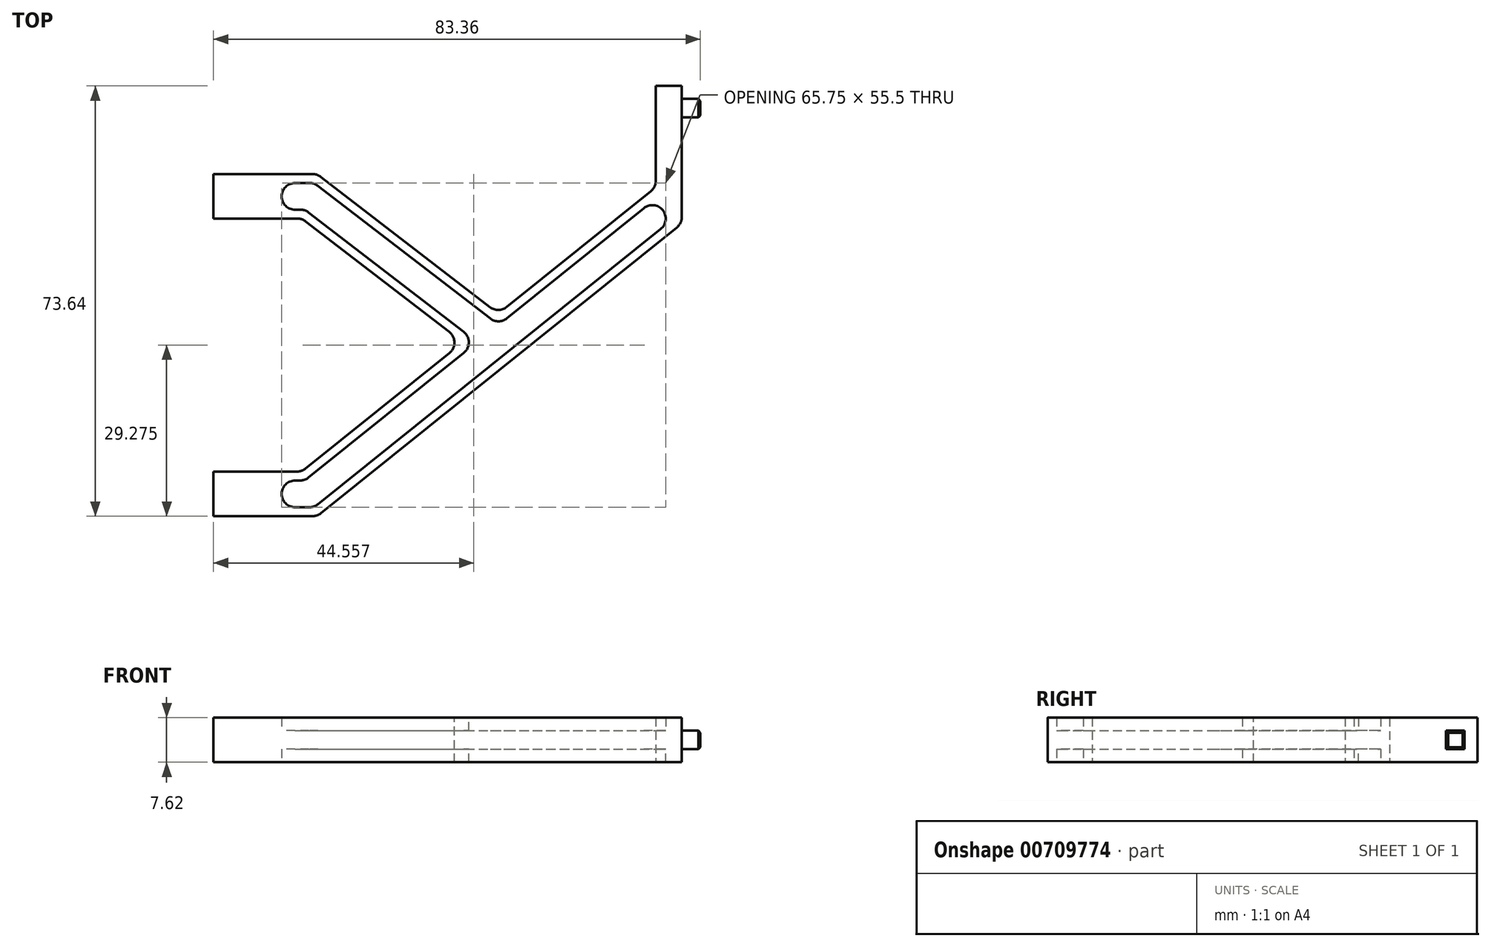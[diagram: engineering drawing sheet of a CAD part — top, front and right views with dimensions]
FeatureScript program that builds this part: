
annotation { "Feature Type Name" : "Feature", "Feature Type Description" : "" }
export const myFeature = defineFeature(function(context is Context, id is Id, definition is map)
    precondition{}
    {
        {
            var Q0;
            Q0=qCreatedBy(makeId("Top.planeOp"),FACE);
            var sketch = newSketch(context, id + "F0", { "sketchPlane" : qUnion([Q0])});
            skLineSegment(sketch, "E0", {"start": v(0, 10.36) * mm, "end": v(17.78, 10.36) * mm});
            skLineSegment(sketch, "E1", {"start": v(0, 68.9) * mm, "end": v(17.78, 68.9) * mm});
            skLineSegment(sketch, "E2", {"start": v(17.78, 68.9) * mm, "end": v(48.79, 45.03) * mm});
            skLineSegment(sketch, "E3", {"start": v(17.78, 10.36) * mm, "end": v(80.19, 60.46) * mm});
            skLineSegment(sketch, "E4", {"start": v(0, 10.36) * mm, "end": v(0, 17.98) * mm});
            skLineSegment(sketch, "E5", {"start": v(17.78, 20.13) * mm, "end": v(42.67, 40.12) * mm});
            skLineSegment(sketch, "E6", {"start": v(0, 68.9) * mm, "end": v(0, 61.29) * mm});
            skLineSegment(sketch, "E7", {"start": v(15.5, 61.04) * mm, "end": v(42.67, 40.12) * mm});
            skLineSegment(sketch, "E8", {"start": v(0, 17.98) * mm, "end": v(15.1, 17.98) * mm});
            skLineSegment(sketch, "E9", {"start": v(17.78, 20.13) * mm, "end": v(15.1, 17.98) * mm});
            skLineSegment(sketch, "E10", {"start": v(15.5, 61.04) * mm, "end": v(15.19, 61.29) * mm});
            skLineSegment(sketch, "E11", {"start": v(0, 61.29) * mm, "end": v(15.19, 61.29) * mm});
            skLineSegment(sketch, "E12", {"start": v(75.74, 84) * mm, "end": v(75.74, 66.67) * mm});
            skLineSegment(sketch, "E13.trimOffspring", {"start": v(48.79, 45.03) * mm, "end": v(75.74, 66.67) * mm});
            skLineSegment(sketch, "E14", {"start": v(75.74, 84) * mm, "end": v(80.19, 84) * mm});
            skLineSegment(sketch, "E15", {"start": v(17.26, 67.38) * mm, "end": v(48.8, 43.09) * mm});
            skLineSegment(sketch, "E16", {"start": v(15.7, 62.81) * mm, "end": v(45.14, 40.14) * mm});
            skLineSegment(sketch, "E17", {"start": v(11.68, 67.38) * mm, "end": v(17.26, 67.38) * mm});
            skLineSegment(sketch, "E18", {"start": v(11.68, 62.81) * mm, "end": v(15.7, 62.81) * mm});
            skLineSegment(sketch, "E19", {"start": v(80.19, 84) * mm, "end": v(80.19, 60.46) * mm});
            skLineSegment(sketch, "E20.trimOffspring", {"start": v(11.68, 67.38) * mm, "end": v(11.68, 62.81) * mm});
            skLineSegment(sketch, "E21", {"start": v(15.64, 16.46) * mm, "end": v(45.14, 40.14) * mm});
            skLineSegment(sketch, "E22", {"start": v(17.24, 11.89) * mm, "end": v(78.37, 60.96) * mm});
            skLineSegment(sketch, "E23", {"start": v(11.68, 16.46) * mm, "end": v(15.64, 16.46) * mm});
            skLineSegment(sketch, "E24", {"start": v(11.68, 11.89) * mm, "end": v(17.24, 11.89) * mm});
            skLineSegment(sketch, "E25", {"start": v(11.68, 16.46) * mm, "end": v(11.68, 11.89) * mm});
            skLineSegment(sketch, "E26.trimOffspring", {"start": v(48.8, 43.09) * mm, "end": v(75.5, 64.53) * mm});
            skLineSegment(sketch, "E27.trimOffspring", {"start": v(75.5, 64.53) * mm, "end": v(78.37, 60.96) * mm});
            skLineSegment(sketch, "E28", {"start": v(80.19, 81.78) * mm, "end": v(83.36, 81.78) * mm});
            skLineSegment(sketch, "E29", {"start": v(83.36, 81.78) * mm, "end": v(83.36, 78.6) * mm});
            skLineSegment(sketch, "E30", {"start": v(83.36, 78.6) * mm, "end": v(80.19, 78.6) * mm});
            skSolve(sketch);
        }
        {
            var Q0;
            Q0=makeQuery(id+"F0.imprint","IMPRINT",FACE,{"disambiguationData":[TD([[makeQuery(id+"F0.imprint","IMPRINT",EDGE,{"derivedFrom":sQuery(id+"F0.wireOp",EDGE,"E0")}),1.0]])]});
            extrude(context, id + "F1", {"entities" : qUnion([Q0]), "depth" : 7.62 * mm, "offsetDistance" : 25.4 * mm, "symmetric" : true});
        }
        {
            var Q0;
            Q0=makeQuery(id+"F0.imprint","IMPRINT",FACE,{"disambiguationData":[TD([[makeQuery(id+"F0.imprint","IMPRINT",EDGE,{"derivedFrom":sQuery(id+"F0.wireOp",EDGE,"E15")}),-1.0]])]});
            extrude(context, id + "F2", {"entities" : qUnion([Q0]), "operationType" : NewBodyOperationType.ADD, "depth" : 3.17 * mm, "offsetDistance" : 25.4 * mm, "symmetric" : true});
        }
        {
            var Q0;
            {var subQ0=sQuery(id+"F0.wireOp",EDGE,"E28");Q0=makeQuery(id+"F0.imprint","IMPRINT",FACE,{"disambiguationData":[TD([[makeQuery(id+"F0.imprint","IMPRINT",EDGE,{"derivedFrom":subQ0}),-1.0]])]});}
            extrude(context, id + "F3", {"entities" : qUnion([Q0]), "operationType" : NewBodyOperationType.ADD, "depth" : 3.17 * mm, "offsetDistance" : 25.4 * mm, "symmetric" : true});
        }
        {
            var Q0;
            Q0=makeQuery(id+"F1.opExtrude","SWEPT_EDGE",EDGE,{"disambiguationData":[OSD([sQuery(id+"F0.wireOp",EDGE,"E10"),sQuery(id+"F0.wireOp",EDGE,"E11")])]});
            var Q1;
            {var subQ0=sQuery(id+"F0.wireOp",EDGE,"E27.trimOffspring");var subQ1=sQuery(id+"F0.wireOp",EDGE,"E26.trimOffspring");var subQ2=sQuery(id+"F0.wireOp",EDGE,"E25");var subQ3=sQuery(id+"F0.wireOp",EDGE,"E24");var subQ4=sQuery(id+"F0.wireOp",EDGE,"E23");var subQ5=sQuery(id+"F0.wireOp",EDGE,"E22");var subQ6=sQuery(id+"F0.wireOp",EDGE,"E21");var subQ7=sQuery(id+"F0.wireOp",EDGE,"E20.trimOffspring");var subQ8=sQuery(id+"F0.wireOp",EDGE,"E18");var subQ9=sQuery(id+"F0.wireOp",EDGE,"E17");var subQ10=sQuery(id+"F0.wireOp",EDGE,"E16");var subQ11=sQuery(id+"F0.wireOp",EDGE,"E15");Q1=makeQuery(id+"F2.boolean.opBoolean","SPLIT",EDGE,{"disambiguationData":[TD([makeQuery(id+"F2.opExtrude","CAP_FACE",FACE,{"disambiguationData":[OSD([subQ11,subQ10,subQ9,subQ8,subQ7,subQ6,subQ5,subQ4,subQ3,subQ2,subQ1,subQ0])],"isStart":false})])],"derivedFrom":makeQuery(id+"F1.opExtrude","SWEPT_EDGE",EDGE,{"disambiguationData":[OSD([subQ8,subQ7])]})});}
            var Q2;
            {var subQ0=sQuery(id+"F0.wireOp",EDGE,"E27.trimOffspring");var subQ1=sQuery(id+"F0.wireOp",EDGE,"E26.trimOffspring");var subQ2=sQuery(id+"F0.wireOp",EDGE,"E25");var subQ3=sQuery(id+"F0.wireOp",EDGE,"E24");var subQ4=sQuery(id+"F0.wireOp",EDGE,"E23");var subQ5=sQuery(id+"F0.wireOp",EDGE,"E22");var subQ6=sQuery(id+"F0.wireOp",EDGE,"E21");var subQ7=sQuery(id+"F0.wireOp",EDGE,"E20.trimOffspring");var subQ8=sQuery(id+"F0.wireOp",EDGE,"E18");var subQ9=sQuery(id+"F0.wireOp",EDGE,"E17");var subQ10=sQuery(id+"F0.wireOp",EDGE,"E16");var subQ11=sQuery(id+"F0.wireOp",EDGE,"E15");Q2=makeQuery(id+"F2.boolean.opBoolean","SPLIT",EDGE,{"disambiguationData":[TD([makeQuery(id+"F2.opExtrude","CAP_FACE",FACE,{"disambiguationData":[OSD([subQ11,subQ10,subQ9,subQ8,subQ7,subQ6,subQ5,subQ4,subQ3,subQ2,subQ1,subQ0])],"isStart":false})])],"derivedFrom":makeQuery(id+"F1.opExtrude","SWEPT_EDGE",EDGE,{"disambiguationData":[OSD([subQ10,subQ8])]})});}
            var Q3;
            {var subQ0=sQuery(id+"F0.wireOp",EDGE,"E27.trimOffspring");var subQ1=sQuery(id+"F0.wireOp",EDGE,"E26.trimOffspring");var subQ2=sQuery(id+"F0.wireOp",EDGE,"E25");var subQ3=sQuery(id+"F0.wireOp",EDGE,"E24");var subQ4=sQuery(id+"F0.wireOp",EDGE,"E23");var subQ5=sQuery(id+"F0.wireOp",EDGE,"E22");var subQ6=sQuery(id+"F0.wireOp",EDGE,"E21");var subQ7=sQuery(id+"F0.wireOp",EDGE,"E20.trimOffspring");var subQ8=sQuery(id+"F0.wireOp",EDGE,"E18");var subQ9=sQuery(id+"F0.wireOp",EDGE,"E17");var subQ10=sQuery(id+"F0.wireOp",EDGE,"E16");var subQ11=sQuery(id+"F0.wireOp",EDGE,"E15");Q3=makeQuery(id+"F2.boolean.opBoolean","SPLIT",EDGE,{"disambiguationData":[TD([makeQuery(id+"F2.opExtrude","CAP_FACE",FACE,{"disambiguationData":[OSD([subQ11,subQ10,subQ9,subQ8,subQ7,subQ6,subQ5,subQ4,subQ3,subQ2,subQ1,subQ0])],"isStart":false})])],"derivedFrom":makeQuery(id+"F1.opExtrude","SWEPT_EDGE",EDGE,{"disambiguationData":[OSD([subQ9,subQ7])]})});}
            var Q4;
            {var subQ0=sQuery(id+"F0.wireOp",EDGE,"E27.trimOffspring");var subQ1=sQuery(id+"F0.wireOp",EDGE,"E26.trimOffspring");var subQ2=sQuery(id+"F0.wireOp",EDGE,"E25");var subQ3=sQuery(id+"F0.wireOp",EDGE,"E24");var subQ4=sQuery(id+"F0.wireOp",EDGE,"E23");var subQ5=sQuery(id+"F0.wireOp",EDGE,"E22");var subQ6=sQuery(id+"F0.wireOp",EDGE,"E21");var subQ7=sQuery(id+"F0.wireOp",EDGE,"E20.trimOffspring");var subQ8=sQuery(id+"F0.wireOp",EDGE,"E18");var subQ9=sQuery(id+"F0.wireOp",EDGE,"E17");var subQ10=sQuery(id+"F0.wireOp",EDGE,"E16");var subQ11=sQuery(id+"F0.wireOp",EDGE,"E15");Q4=makeQuery(id+"F2.boolean.opBoolean","SPLIT",EDGE,{"disambiguationData":[TD([makeQuery(id+"F2.opExtrude","CAP_FACE",FACE,{"disambiguationData":[OSD([subQ11,subQ10,subQ9,subQ8,subQ7,subQ6,subQ5,subQ4,subQ3,subQ2,subQ1,subQ0])],"isStart":false})])],"derivedFrom":makeQuery(id+"F1.opExtrude","SWEPT_EDGE",EDGE,{"disambiguationData":[OSD([subQ11,subQ9])]})});}
            var Q5;
            Q5=makeQuery(id+"F1.opExtrude","SWEPT_EDGE",EDGE,{"disambiguationData":[OSD([sQuery(id+"F0.wireOp",EDGE,"E1"),sQuery(id+"F0.wireOp",EDGE,"E2")])]});
            var Q6;
            {var subQ0=sQuery(id+"F0.wireOp",EDGE,"E27.trimOffspring");var subQ1=sQuery(id+"F0.wireOp",EDGE,"E26.trimOffspring");var subQ2=sQuery(id+"F0.wireOp",EDGE,"E25");var subQ3=sQuery(id+"F0.wireOp",EDGE,"E24");var subQ4=sQuery(id+"F0.wireOp",EDGE,"E23");var subQ5=sQuery(id+"F0.wireOp",EDGE,"E22");var subQ6=sQuery(id+"F0.wireOp",EDGE,"E21");var subQ7=sQuery(id+"F0.wireOp",EDGE,"E20.trimOffspring");var subQ8=sQuery(id+"F0.wireOp",EDGE,"E18");var subQ9=sQuery(id+"F0.wireOp",EDGE,"E17");var subQ10=sQuery(id+"F0.wireOp",EDGE,"E16");var subQ11=sQuery(id+"F0.wireOp",EDGE,"E15");Q6=makeQuery(id+"F2.boolean.opBoolean","SPLIT",EDGE,{"disambiguationData":[TD([makeQuery(id+"F2.opExtrude","CAP_FACE",FACE,{"disambiguationData":[OSD([subQ11,subQ10,subQ9,subQ8,subQ7,subQ6,subQ5,subQ4,subQ3,subQ2,subQ1,subQ0])],"isStart":true})])],"derivedFrom":makeQuery(id+"F1.opExtrude","SWEPT_EDGE",EDGE,{"disambiguationData":[OSD([subQ10,subQ8])]})});}
            var Q7;
            {var subQ0=sQuery(id+"F0.wireOp",EDGE,"E27.trimOffspring");var subQ1=sQuery(id+"F0.wireOp",EDGE,"E26.trimOffspring");var subQ2=sQuery(id+"F0.wireOp",EDGE,"E25");var subQ3=sQuery(id+"F0.wireOp",EDGE,"E24");var subQ4=sQuery(id+"F0.wireOp",EDGE,"E23");var subQ5=sQuery(id+"F0.wireOp",EDGE,"E22");var subQ6=sQuery(id+"F0.wireOp",EDGE,"E21");var subQ7=sQuery(id+"F0.wireOp",EDGE,"E20.trimOffspring");var subQ8=sQuery(id+"F0.wireOp",EDGE,"E18");var subQ9=sQuery(id+"F0.wireOp",EDGE,"E17");var subQ10=sQuery(id+"F0.wireOp",EDGE,"E16");var subQ11=sQuery(id+"F0.wireOp",EDGE,"E15");Q7=makeQuery(id+"F2.boolean.opBoolean","SPLIT",EDGE,{"disambiguationData":[TD([makeQuery(id+"F2.opExtrude","CAP_FACE",FACE,{"disambiguationData":[OSD([subQ11,subQ10,subQ9,subQ8,subQ7,subQ6,subQ5,subQ4,subQ3,subQ2,subQ1,subQ0])],"isStart":true})])],"derivedFrom":makeQuery(id+"F1.opExtrude","SWEPT_EDGE",EDGE,{"disambiguationData":[OSD([subQ8,subQ7])]})});}
            var Q8;
            {var subQ0=sQuery(id+"F0.wireOp",EDGE,"E27.trimOffspring");var subQ1=sQuery(id+"F0.wireOp",EDGE,"E26.trimOffspring");var subQ2=sQuery(id+"F0.wireOp",EDGE,"E25");var subQ3=sQuery(id+"F0.wireOp",EDGE,"E24");var subQ4=sQuery(id+"F0.wireOp",EDGE,"E23");var subQ5=sQuery(id+"F0.wireOp",EDGE,"E22");var subQ6=sQuery(id+"F0.wireOp",EDGE,"E21");var subQ7=sQuery(id+"F0.wireOp",EDGE,"E20.trimOffspring");var subQ8=sQuery(id+"F0.wireOp",EDGE,"E18");var subQ9=sQuery(id+"F0.wireOp",EDGE,"E17");var subQ10=sQuery(id+"F0.wireOp",EDGE,"E16");var subQ11=sQuery(id+"F0.wireOp",EDGE,"E15");Q8=makeQuery(id+"F2.boolean.opBoolean","SPLIT",EDGE,{"disambiguationData":[TD([makeQuery(id+"F2.opExtrude","CAP_FACE",FACE,{"disambiguationData":[OSD([subQ11,subQ10,subQ9,subQ8,subQ7,subQ6,subQ5,subQ4,subQ3,subQ2,subQ1,subQ0])],"isStart":true})])],"derivedFrom":makeQuery(id+"F1.opExtrude","SWEPT_EDGE",EDGE,{"disambiguationData":[OSD([subQ9,subQ7])]})});}
            var Q9;
            {var subQ0=sQuery(id+"F0.wireOp",EDGE,"E27.trimOffspring");var subQ1=sQuery(id+"F0.wireOp",EDGE,"E26.trimOffspring");var subQ2=sQuery(id+"F0.wireOp",EDGE,"E25");var subQ3=sQuery(id+"F0.wireOp",EDGE,"E24");var subQ4=sQuery(id+"F0.wireOp",EDGE,"E23");var subQ5=sQuery(id+"F0.wireOp",EDGE,"E22");var subQ6=sQuery(id+"F0.wireOp",EDGE,"E21");var subQ7=sQuery(id+"F0.wireOp",EDGE,"E20.trimOffspring");var subQ8=sQuery(id+"F0.wireOp",EDGE,"E18");var subQ9=sQuery(id+"F0.wireOp",EDGE,"E17");var subQ10=sQuery(id+"F0.wireOp",EDGE,"E16");var subQ11=sQuery(id+"F0.wireOp",EDGE,"E15");Q9=makeQuery(id+"F2.boolean.opBoolean","SPLIT",EDGE,{"disambiguationData":[TD([makeQuery(id+"F2.opExtrude","CAP_FACE",FACE,{"disambiguationData":[OSD([subQ11,subQ10,subQ9,subQ8,subQ7,subQ6,subQ5,subQ4,subQ3,subQ2,subQ1,subQ0])],"isStart":true})])],"derivedFrom":makeQuery(id+"F1.opExtrude","SWEPT_EDGE",EDGE,{"disambiguationData":[OSD([subQ11,subQ9])]})});}
            var Q10;
            {var subQ0=sQuery(id+"F0.wireOp",EDGE,"E27.trimOffspring");var subQ1=sQuery(id+"F0.wireOp",EDGE,"E26.trimOffspring");var subQ2=sQuery(id+"F0.wireOp",EDGE,"E25");var subQ3=sQuery(id+"F0.wireOp",EDGE,"E24");var subQ4=sQuery(id+"F0.wireOp",EDGE,"E23");var subQ5=sQuery(id+"F0.wireOp",EDGE,"E22");var subQ6=sQuery(id+"F0.wireOp",EDGE,"E21");var subQ7=sQuery(id+"F0.wireOp",EDGE,"E20.trimOffspring");var subQ8=sQuery(id+"F0.wireOp",EDGE,"E18");var subQ9=sQuery(id+"F0.wireOp",EDGE,"E17");var subQ10=sQuery(id+"F0.wireOp",EDGE,"E16");var subQ11=sQuery(id+"F0.wireOp",EDGE,"E15");Q10=makeQuery(id+"F2.boolean.opBoolean","SPLIT",EDGE,{"disambiguationData":[TD([makeQuery(id+"F2.opExtrude","CAP_FACE",FACE,{"disambiguationData":[OSD([subQ11,subQ10,subQ9,subQ8,subQ7,subQ6,subQ5,subQ4,subQ3,subQ2,subQ1,subQ0])],"isStart":false})])],"derivedFrom":makeQuery(id+"F1.opExtrude","SWEPT_EDGE",EDGE,{"disambiguationData":[OSD([subQ11,subQ1])]})});}
            var Q11;
            {var subQ0=sQuery(id+"F0.wireOp",EDGE,"E27.trimOffspring");var subQ1=sQuery(id+"F0.wireOp",EDGE,"E26.trimOffspring");var subQ2=sQuery(id+"F0.wireOp",EDGE,"E25");var subQ3=sQuery(id+"F0.wireOp",EDGE,"E24");var subQ4=sQuery(id+"F0.wireOp",EDGE,"E23");var subQ5=sQuery(id+"F0.wireOp",EDGE,"E22");var subQ6=sQuery(id+"F0.wireOp",EDGE,"E21");var subQ7=sQuery(id+"F0.wireOp",EDGE,"E20.trimOffspring");var subQ8=sQuery(id+"F0.wireOp",EDGE,"E18");var subQ9=sQuery(id+"F0.wireOp",EDGE,"E17");var subQ10=sQuery(id+"F0.wireOp",EDGE,"E16");var subQ11=sQuery(id+"F0.wireOp",EDGE,"E15");Q11=makeQuery(id+"F2.boolean.opBoolean","SPLIT",EDGE,{"disambiguationData":[TD([makeQuery(id+"F2.opExtrude","CAP_FACE",FACE,{"disambiguationData":[OSD([subQ11,subQ10,subQ9,subQ8,subQ7,subQ6,subQ5,subQ4,subQ3,subQ2,subQ1,subQ0])],"isStart":false})])],"derivedFrom":makeQuery(id+"F1.opExtrude","SWEPT_EDGE",EDGE,{"disambiguationData":[OSD([subQ10,subQ6])]})});}
            var Q12;
            Q12=makeQuery(id+"F1.opExtrude","SWEPT_EDGE",EDGE,{"disambiguationData":[OSD([sQuery(id+"F0.wireOp",EDGE,"E5"),sQuery(id+"F0.wireOp",EDGE,"E7")])]});
            var Q13;
            Q13=makeQuery(id+"F1.opExtrude","SWEPT_EDGE",EDGE,{"disambiguationData":[OSD([sQuery(id+"F0.wireOp",EDGE,"E2"),sQuery(id+"F0.wireOp",EDGE,"E13.trimOffspring")])]});
            var Q14;
            {var subQ0=sQuery(id+"F0.wireOp",EDGE,"E27.trimOffspring");var subQ1=sQuery(id+"F0.wireOp",EDGE,"E26.trimOffspring");var subQ2=sQuery(id+"F0.wireOp",EDGE,"E25");var subQ3=sQuery(id+"F0.wireOp",EDGE,"E24");var subQ4=sQuery(id+"F0.wireOp",EDGE,"E23");var subQ5=sQuery(id+"F0.wireOp",EDGE,"E22");var subQ6=sQuery(id+"F0.wireOp",EDGE,"E21");var subQ7=sQuery(id+"F0.wireOp",EDGE,"E20.trimOffspring");var subQ8=sQuery(id+"F0.wireOp",EDGE,"E18");var subQ9=sQuery(id+"F0.wireOp",EDGE,"E17");var subQ10=sQuery(id+"F0.wireOp",EDGE,"E16");var subQ11=sQuery(id+"F0.wireOp",EDGE,"E15");Q14=makeQuery(id+"F2.boolean.opBoolean","SPLIT",EDGE,{"disambiguationData":[TD([makeQuery(id+"F2.opExtrude","CAP_FACE",FACE,{"disambiguationData":[OSD([subQ11,subQ10,subQ9,subQ8,subQ7,subQ6,subQ5,subQ4,subQ3,subQ2,subQ1,subQ0])],"isStart":true})])],"derivedFrom":makeQuery(id+"F1.opExtrude","SWEPT_EDGE",EDGE,{"disambiguationData":[OSD([subQ11,subQ1])]})});}
            var Q15;
            {var subQ0=sQuery(id+"F0.wireOp",EDGE,"E27.trimOffspring");var subQ1=sQuery(id+"F0.wireOp",EDGE,"E26.trimOffspring");var subQ2=sQuery(id+"F0.wireOp",EDGE,"E25");var subQ3=sQuery(id+"F0.wireOp",EDGE,"E24");var subQ4=sQuery(id+"F0.wireOp",EDGE,"E23");var subQ5=sQuery(id+"F0.wireOp",EDGE,"E22");var subQ6=sQuery(id+"F0.wireOp",EDGE,"E21");var subQ7=sQuery(id+"F0.wireOp",EDGE,"E20.trimOffspring");var subQ8=sQuery(id+"F0.wireOp",EDGE,"E18");var subQ9=sQuery(id+"F0.wireOp",EDGE,"E17");var subQ10=sQuery(id+"F0.wireOp",EDGE,"E16");var subQ11=sQuery(id+"F0.wireOp",EDGE,"E15");Q15=makeQuery(id+"F2.boolean.opBoolean","SPLIT",EDGE,{"disambiguationData":[TD([makeQuery(id+"F2.opExtrude","CAP_FACE",FACE,{"disambiguationData":[OSD([subQ11,subQ10,subQ9,subQ8,subQ7,subQ6,subQ5,subQ4,subQ3,subQ2,subQ1,subQ0])],"isStart":true})])],"derivedFrom":makeQuery(id+"F1.opExtrude","SWEPT_EDGE",EDGE,{"disambiguationData":[OSD([subQ10,subQ6])]})});}
            var Q16;
            {var subQ0=sQuery(id+"F0.wireOp",EDGE,"E27.trimOffspring");var subQ1=sQuery(id+"F0.wireOp",EDGE,"E26.trimOffspring");var subQ2=sQuery(id+"F0.wireOp",EDGE,"E25");var subQ3=sQuery(id+"F0.wireOp",EDGE,"E24");var subQ4=sQuery(id+"F0.wireOp",EDGE,"E23");var subQ5=sQuery(id+"F0.wireOp",EDGE,"E22");var subQ6=sQuery(id+"F0.wireOp",EDGE,"E21");var subQ7=sQuery(id+"F0.wireOp",EDGE,"E20.trimOffspring");var subQ8=sQuery(id+"F0.wireOp",EDGE,"E18");var subQ9=sQuery(id+"F0.wireOp",EDGE,"E17");var subQ10=sQuery(id+"F0.wireOp",EDGE,"E16");var subQ11=sQuery(id+"F0.wireOp",EDGE,"E15");Q16=makeQuery(id+"F2.boolean.opBoolean","SPLIT",EDGE,{"disambiguationData":[TD([makeQuery(id+"F2.opExtrude","CAP_FACE",FACE,{"disambiguationData":[OSD([subQ11,subQ10,subQ9,subQ8,subQ7,subQ6,subQ5,subQ4,subQ3,subQ2,subQ1,subQ0])],"isStart":true})])],"derivedFrom":makeQuery(id+"F1.opExtrude","SWEPT_EDGE",EDGE,{"disambiguationData":[OSD([subQ1,subQ0])]})});}
            var Q17;
            {var subQ0=sQuery(id+"F0.wireOp",EDGE,"E27.trimOffspring");var subQ1=sQuery(id+"F0.wireOp",EDGE,"E26.trimOffspring");var subQ2=sQuery(id+"F0.wireOp",EDGE,"E25");var subQ3=sQuery(id+"F0.wireOp",EDGE,"E24");var subQ4=sQuery(id+"F0.wireOp",EDGE,"E23");var subQ5=sQuery(id+"F0.wireOp",EDGE,"E22");var subQ6=sQuery(id+"F0.wireOp",EDGE,"E21");var subQ7=sQuery(id+"F0.wireOp",EDGE,"E20.trimOffspring");var subQ8=sQuery(id+"F0.wireOp",EDGE,"E18");var subQ9=sQuery(id+"F0.wireOp",EDGE,"E17");var subQ10=sQuery(id+"F0.wireOp",EDGE,"E16");var subQ11=sQuery(id+"F0.wireOp",EDGE,"E15");Q17=makeQuery(id+"F2.boolean.opBoolean","SPLIT",EDGE,{"disambiguationData":[TD([makeQuery(id+"F2.opExtrude","CAP_FACE",FACE,{"disambiguationData":[OSD([subQ11,subQ10,subQ9,subQ8,subQ7,subQ6,subQ5,subQ4,subQ3,subQ2,subQ1,subQ0])],"isStart":true})])],"derivedFrom":makeQuery(id+"F1.opExtrude","SWEPT_EDGE",EDGE,{"disambiguationData":[OSD([subQ5,subQ0])]})});}
            var Q18;
            Q18=makeQuery(id+"F1.opExtrude","SWEPT_EDGE",EDGE,{"disambiguationData":[OSD([sQuery(id+"F0.wireOp",EDGE,"E3"),sQuery(id+"F0.wireOp",EDGE,"E19")])]});
            var Q19;
            Q19=makeQuery(id+"F1.opExtrude","SWEPT_EDGE",EDGE,{"disambiguationData":[OSD([sQuery(id+"F0.wireOp",EDGE,"E12"),sQuery(id+"F0.wireOp",EDGE,"E13.trimOffspring")])]});
            var Q20;
            {var subQ0=sQuery(id+"F0.wireOp",EDGE,"E27.trimOffspring");var subQ1=sQuery(id+"F0.wireOp",EDGE,"E26.trimOffspring");var subQ2=sQuery(id+"F0.wireOp",EDGE,"E25");var subQ3=sQuery(id+"F0.wireOp",EDGE,"E24");var subQ4=sQuery(id+"F0.wireOp",EDGE,"E23");var subQ5=sQuery(id+"F0.wireOp",EDGE,"E22");var subQ6=sQuery(id+"F0.wireOp",EDGE,"E21");var subQ7=sQuery(id+"F0.wireOp",EDGE,"E20.trimOffspring");var subQ8=sQuery(id+"F0.wireOp",EDGE,"E18");var subQ9=sQuery(id+"F0.wireOp",EDGE,"E17");var subQ10=sQuery(id+"F0.wireOp",EDGE,"E16");var subQ11=sQuery(id+"F0.wireOp",EDGE,"E15");Q20=makeQuery(id+"F2.boolean.opBoolean","SPLIT",EDGE,{"disambiguationData":[TD([makeQuery(id+"F2.opExtrude","CAP_FACE",FACE,{"disambiguationData":[OSD([subQ11,subQ10,subQ9,subQ8,subQ7,subQ6,subQ5,subQ4,subQ3,subQ2,subQ1,subQ0])],"isStart":false})])],"derivedFrom":makeQuery(id+"F1.opExtrude","SWEPT_EDGE",EDGE,{"disambiguationData":[OSD([subQ5,subQ0])]})});}
            var Q21;
            {var subQ0=sQuery(id+"F0.wireOp",EDGE,"E27.trimOffspring");var subQ1=sQuery(id+"F0.wireOp",EDGE,"E26.trimOffspring");var subQ2=sQuery(id+"F0.wireOp",EDGE,"E25");var subQ3=sQuery(id+"F0.wireOp",EDGE,"E24");var subQ4=sQuery(id+"F0.wireOp",EDGE,"E23");var subQ5=sQuery(id+"F0.wireOp",EDGE,"E22");var subQ6=sQuery(id+"F0.wireOp",EDGE,"E21");var subQ7=sQuery(id+"F0.wireOp",EDGE,"E20.trimOffspring");var subQ8=sQuery(id+"F0.wireOp",EDGE,"E18");var subQ9=sQuery(id+"F0.wireOp",EDGE,"E17");var subQ10=sQuery(id+"F0.wireOp",EDGE,"E16");var subQ11=sQuery(id+"F0.wireOp",EDGE,"E15");Q21=makeQuery(id+"F2.boolean.opBoolean","SPLIT",EDGE,{"disambiguationData":[TD([makeQuery(id+"F2.opExtrude","CAP_FACE",FACE,{"disambiguationData":[OSD([subQ11,subQ10,subQ9,subQ8,subQ7,subQ6,subQ5,subQ4,subQ3,subQ2,subQ1,subQ0])],"isStart":false})])],"derivedFrom":makeQuery(id+"F1.opExtrude","SWEPT_EDGE",EDGE,{"disambiguationData":[OSD([subQ1,subQ0])]})});}
            var Q22;
            {var subQ0=sQuery(id+"F0.wireOp",EDGE,"E27.trimOffspring");var subQ1=sQuery(id+"F0.wireOp",EDGE,"E26.trimOffspring");var subQ2=sQuery(id+"F0.wireOp",EDGE,"E25");var subQ3=sQuery(id+"F0.wireOp",EDGE,"E24");var subQ4=sQuery(id+"F0.wireOp",EDGE,"E23");var subQ5=sQuery(id+"F0.wireOp",EDGE,"E22");var subQ6=sQuery(id+"F0.wireOp",EDGE,"E21");var subQ7=sQuery(id+"F0.wireOp",EDGE,"E20.trimOffspring");var subQ8=sQuery(id+"F0.wireOp",EDGE,"E18");var subQ9=sQuery(id+"F0.wireOp",EDGE,"E17");var subQ10=sQuery(id+"F0.wireOp",EDGE,"E16");var subQ11=sQuery(id+"F0.wireOp",EDGE,"E15");Q22=makeQuery(id+"F2.boolean.opBoolean","SPLIT",EDGE,{"disambiguationData":[TD([makeQuery(id+"F2.opExtrude","CAP_FACE",FACE,{"disambiguationData":[OSD([subQ11,subQ10,subQ9,subQ8,subQ7,subQ6,subQ5,subQ4,subQ3,subQ2,subQ1,subQ0])],"isStart":false})])],"derivedFrom":makeQuery(id+"F1.opExtrude","SWEPT_EDGE",EDGE,{"disambiguationData":[OSD([subQ6,subQ4])]})});}
            var Q23;
            {var subQ0=sQuery(id+"F0.wireOp",EDGE,"E27.trimOffspring");var subQ1=sQuery(id+"F0.wireOp",EDGE,"E26.trimOffspring");var subQ2=sQuery(id+"F0.wireOp",EDGE,"E25");var subQ3=sQuery(id+"F0.wireOp",EDGE,"E24");var subQ4=sQuery(id+"F0.wireOp",EDGE,"E23");var subQ5=sQuery(id+"F0.wireOp",EDGE,"E22");var subQ6=sQuery(id+"F0.wireOp",EDGE,"E21");var subQ7=sQuery(id+"F0.wireOp",EDGE,"E20.trimOffspring");var subQ8=sQuery(id+"F0.wireOp",EDGE,"E18");var subQ9=sQuery(id+"F0.wireOp",EDGE,"E17");var subQ10=sQuery(id+"F0.wireOp",EDGE,"E16");var subQ11=sQuery(id+"F0.wireOp",EDGE,"E15");Q23=makeQuery(id+"F2.boolean.opBoolean","SPLIT",EDGE,{"disambiguationData":[TD([makeQuery(id+"F2.opExtrude","CAP_FACE",FACE,{"disambiguationData":[OSD([subQ11,subQ10,subQ9,subQ8,subQ7,subQ6,subQ5,subQ4,subQ3,subQ2,subQ1,subQ0])],"isStart":false})])],"derivedFrom":makeQuery(id+"F1.opExtrude","SWEPT_EDGE",EDGE,{"disambiguationData":[OSD([subQ4,subQ2])]})});}
            var Q24;
            {var subQ0=sQuery(id+"F0.wireOp",EDGE,"E27.trimOffspring");var subQ1=sQuery(id+"F0.wireOp",EDGE,"E26.trimOffspring");var subQ2=sQuery(id+"F0.wireOp",EDGE,"E25");var subQ3=sQuery(id+"F0.wireOp",EDGE,"E24");var subQ4=sQuery(id+"F0.wireOp",EDGE,"E23");var subQ5=sQuery(id+"F0.wireOp",EDGE,"E22");var subQ6=sQuery(id+"F0.wireOp",EDGE,"E21");var subQ7=sQuery(id+"F0.wireOp",EDGE,"E20.trimOffspring");var subQ8=sQuery(id+"F0.wireOp",EDGE,"E18");var subQ9=sQuery(id+"F0.wireOp",EDGE,"E17");var subQ10=sQuery(id+"F0.wireOp",EDGE,"E16");var subQ11=sQuery(id+"F0.wireOp",EDGE,"E15");Q24=makeQuery(id+"F2.boolean.opBoolean","SPLIT",EDGE,{"disambiguationData":[TD([makeQuery(id+"F2.opExtrude","CAP_FACE",FACE,{"disambiguationData":[OSD([subQ11,subQ10,subQ9,subQ8,subQ7,subQ6,subQ5,subQ4,subQ3,subQ2,subQ1,subQ0])],"isStart":false})])],"derivedFrom":makeQuery(id+"F1.opExtrude","SWEPT_EDGE",EDGE,{"disambiguationData":[OSD([subQ3,subQ2])]})});}
            var Q25;
            {var subQ0=sQuery(id+"F0.wireOp",EDGE,"E27.trimOffspring");var subQ1=sQuery(id+"F0.wireOp",EDGE,"E26.trimOffspring");var subQ2=sQuery(id+"F0.wireOp",EDGE,"E25");var subQ3=sQuery(id+"F0.wireOp",EDGE,"E24");var subQ4=sQuery(id+"F0.wireOp",EDGE,"E23");var subQ5=sQuery(id+"F0.wireOp",EDGE,"E22");var subQ6=sQuery(id+"F0.wireOp",EDGE,"E21");var subQ7=sQuery(id+"F0.wireOp",EDGE,"E20.trimOffspring");var subQ8=sQuery(id+"F0.wireOp",EDGE,"E18");var subQ9=sQuery(id+"F0.wireOp",EDGE,"E17");var subQ10=sQuery(id+"F0.wireOp",EDGE,"E16");var subQ11=sQuery(id+"F0.wireOp",EDGE,"E15");Q25=makeQuery(id+"F2.boolean.opBoolean","SPLIT",EDGE,{"disambiguationData":[TD([makeQuery(id+"F2.opExtrude","CAP_FACE",FACE,{"disambiguationData":[OSD([subQ11,subQ10,subQ9,subQ8,subQ7,subQ6,subQ5,subQ4,subQ3,subQ2,subQ1,subQ0])],"isStart":false})])],"derivedFrom":makeQuery(id+"F1.opExtrude","SWEPT_EDGE",EDGE,{"disambiguationData":[OSD([subQ5,subQ3])]})});}
            var Q26;
            {var subQ0=sQuery(id+"F0.wireOp",EDGE,"E27.trimOffspring");var subQ1=sQuery(id+"F0.wireOp",EDGE,"E26.trimOffspring");var subQ2=sQuery(id+"F0.wireOp",EDGE,"E25");var subQ3=sQuery(id+"F0.wireOp",EDGE,"E24");var subQ4=sQuery(id+"F0.wireOp",EDGE,"E23");var subQ5=sQuery(id+"F0.wireOp",EDGE,"E22");var subQ6=sQuery(id+"F0.wireOp",EDGE,"E21");var subQ7=sQuery(id+"F0.wireOp",EDGE,"E20.trimOffspring");var subQ8=sQuery(id+"F0.wireOp",EDGE,"E18");var subQ9=sQuery(id+"F0.wireOp",EDGE,"E17");var subQ10=sQuery(id+"F0.wireOp",EDGE,"E16");var subQ11=sQuery(id+"F0.wireOp",EDGE,"E15");Q26=makeQuery(id+"F2.boolean.opBoolean","SPLIT",EDGE,{"disambiguationData":[TD([makeQuery(id+"F2.opExtrude","CAP_FACE",FACE,{"disambiguationData":[OSD([subQ11,subQ10,subQ9,subQ8,subQ7,subQ6,subQ5,subQ4,subQ3,subQ2,subQ1,subQ0])],"isStart":true})])],"derivedFrom":makeQuery(id+"F1.opExtrude","SWEPT_EDGE",EDGE,{"disambiguationData":[OSD([subQ4,subQ2])]})});}
            var Q27;
            {var subQ0=sQuery(id+"F0.wireOp",EDGE,"E27.trimOffspring");var subQ1=sQuery(id+"F0.wireOp",EDGE,"E26.trimOffspring");var subQ2=sQuery(id+"F0.wireOp",EDGE,"E25");var subQ3=sQuery(id+"F0.wireOp",EDGE,"E24");var subQ4=sQuery(id+"F0.wireOp",EDGE,"E23");var subQ5=sQuery(id+"F0.wireOp",EDGE,"E22");var subQ6=sQuery(id+"F0.wireOp",EDGE,"E21");var subQ7=sQuery(id+"F0.wireOp",EDGE,"E20.trimOffspring");var subQ8=sQuery(id+"F0.wireOp",EDGE,"E18");var subQ9=sQuery(id+"F0.wireOp",EDGE,"E17");var subQ10=sQuery(id+"F0.wireOp",EDGE,"E16");var subQ11=sQuery(id+"F0.wireOp",EDGE,"E15");Q27=makeQuery(id+"F2.boolean.opBoolean","SPLIT",EDGE,{"disambiguationData":[TD([makeQuery(id+"F2.opExtrude","CAP_FACE",FACE,{"disambiguationData":[OSD([subQ11,subQ10,subQ9,subQ8,subQ7,subQ6,subQ5,subQ4,subQ3,subQ2,subQ1,subQ0])],"isStart":true})])],"derivedFrom":makeQuery(id+"F1.opExtrude","SWEPT_EDGE",EDGE,{"disambiguationData":[OSD([subQ6,subQ4])]})});}
            var Q28;
            {var subQ0=sQuery(id+"F0.wireOp",EDGE,"E27.trimOffspring");var subQ1=sQuery(id+"F0.wireOp",EDGE,"E26.trimOffspring");var subQ2=sQuery(id+"F0.wireOp",EDGE,"E25");var subQ3=sQuery(id+"F0.wireOp",EDGE,"E24");var subQ4=sQuery(id+"F0.wireOp",EDGE,"E23");var subQ5=sQuery(id+"F0.wireOp",EDGE,"E22");var subQ6=sQuery(id+"F0.wireOp",EDGE,"E21");var subQ7=sQuery(id+"F0.wireOp",EDGE,"E20.trimOffspring");var subQ8=sQuery(id+"F0.wireOp",EDGE,"E18");var subQ9=sQuery(id+"F0.wireOp",EDGE,"E17");var subQ10=sQuery(id+"F0.wireOp",EDGE,"E16");var subQ11=sQuery(id+"F0.wireOp",EDGE,"E15");Q28=makeQuery(id+"F2.boolean.opBoolean","SPLIT",EDGE,{"disambiguationData":[TD([makeQuery(id+"F2.opExtrude","CAP_FACE",FACE,{"disambiguationData":[OSD([subQ11,subQ10,subQ9,subQ8,subQ7,subQ6,subQ5,subQ4,subQ3,subQ2,subQ1,subQ0])],"isStart":true})])],"derivedFrom":makeQuery(id+"F1.opExtrude","SWEPT_EDGE",EDGE,{"disambiguationData":[OSD([subQ5,subQ3])]})});}
            var Q29;
            {var subQ0=sQuery(id+"F0.wireOp",EDGE,"E27.trimOffspring");var subQ1=sQuery(id+"F0.wireOp",EDGE,"E26.trimOffspring");var subQ2=sQuery(id+"F0.wireOp",EDGE,"E25");var subQ3=sQuery(id+"F0.wireOp",EDGE,"E24");var subQ4=sQuery(id+"F0.wireOp",EDGE,"E23");var subQ5=sQuery(id+"F0.wireOp",EDGE,"E22");var subQ6=sQuery(id+"F0.wireOp",EDGE,"E21");var subQ7=sQuery(id+"F0.wireOp",EDGE,"E20.trimOffspring");var subQ8=sQuery(id+"F0.wireOp",EDGE,"E18");var subQ9=sQuery(id+"F0.wireOp",EDGE,"E17");var subQ10=sQuery(id+"F0.wireOp",EDGE,"E16");var subQ11=sQuery(id+"F0.wireOp",EDGE,"E15");Q29=makeQuery(id+"F2.boolean.opBoolean","SPLIT",EDGE,{"disambiguationData":[TD([makeQuery(id+"F2.opExtrude","CAP_FACE",FACE,{"disambiguationData":[OSD([subQ11,subQ10,subQ9,subQ8,subQ7,subQ6,subQ5,subQ4,subQ3,subQ2,subQ1,subQ0])],"isStart":true})])],"derivedFrom":makeQuery(id+"F1.opExtrude","SWEPT_EDGE",EDGE,{"disambiguationData":[OSD([subQ3,subQ2])]})});}
            var Q30;
            Q30=makeQuery(id+"F1.opExtrude","SWEPT_EDGE",EDGE,{"disambiguationData":[OSD([sQuery(id+"F0.wireOp",EDGE,"E0"),sQuery(id+"F0.wireOp",EDGE,"E3")])]});
            var Q31;
            Q31=makeQuery(id+"F1.opExtrude","SWEPT_EDGE",EDGE,{"disambiguationData":[OSD([sQuery(id+"F0.wireOp",EDGE,"E8"),sQuery(id+"F0.wireOp",EDGE,"E9")])]});
            fillet(context, id + "F4", {"entities" : qUnion([Q0, Q1, Q2, Q3, Q4, Q5, Q6, Q7, Q8, Q9, Q10, Q11, Q12, Q13, Q14, Q15, Q16, Q17, Q18, Q19, Q20, Q21, Q22, Q23, Q24, Q25, Q26, Q27, Q28, Q29, Q30, Q31]), "radius" : 2.3 * mm, "tangentPropagation" : true, "allowEdgeOverflow" : false});
        }
        {
            var Q0;
            Q0=makeQuery(id+"F3.opExtrude","SWEPT_FACE",FACE,{"disambiguationData":[OSD([sQuery(id+"F0.wireOp",EDGE,"E29")])]});
            chamfer(context, id + "F5", {"entities" : qUnion([Q0]), "width" : 0.33 * mm, "tangentPropagation" : true});
        }
        {
            var Q0;
            Q0=makeQuery(id+"F1.opExtrude","SWEPT_BODY",BODY,{"disambiguationData":[OSD([sQuery(id+"F0.wireOp",EDGE,"E0"),sQuery(id+"F0.wireOp",EDGE,"E1"),sQuery(id+"F0.wireOp",EDGE,"E2"),sQuery(id+"F0.wireOp",EDGE,"E3"),sQuery(id+"F0.wireOp",EDGE,"E4"),sQuery(id+"F0.wireOp",EDGE,"E5"),sQuery(id+"F0.wireOp",EDGE,"E6"),sQuery(id+"F0.wireOp",EDGE,"E7"),sQuery(id+"F0.wireOp",EDGE,"E8"),sQuery(id+"F0.wireOp",EDGE,"E9"),sQuery(id+"F0.wireOp",EDGE,"E10"),sQuery(id+"F0.wireOp",EDGE,"E11"),sQuery(id+"F0.wireOp",EDGE,"E12"),sQuery(id+"F0.wireOp",EDGE,"E13.trimOffspring"),sQuery(id+"F0.wireOp",EDGE,"E14"),sQuery(id+"F0.wireOp",EDGE,"E15"),sQuery(id+"F0.wireOp",EDGE,"E16"),sQuery(id+"F0.wireOp",EDGE,"E17"),sQuery(id+"F0.wireOp",EDGE,"E18"),sQuery(id+"F0.wireOp",EDGE,"E19"),sQuery(id+"F0.wireOp",EDGE,"E20.trimOffspring"),sQuery(id+"F0.wireOp",EDGE,"E21"),sQuery(id+"F0.wireOp",EDGE,"E22"),sQuery(id+"F0.wireOp",EDGE,"E23"),sQuery(id+"F0.wireOp",EDGE,"E24"),sQuery(id+"F0.wireOp",EDGE,"E25"),sQuery(id+"F0.wireOp",EDGE,"E26.trimOffspring"),sQuery(id+"F0.wireOp",EDGE,"E27.trimOffspring")])]});
            transform(context, id + "F6", {"entities" : qUnion([Q0]), "transformType" : TransformType.TRANSLATION_3D, "dx" : 0 * mm, "dy" : 0 * mm, "dz" : 3.8 * mm, "makeCopy" : false});
        }
    });
